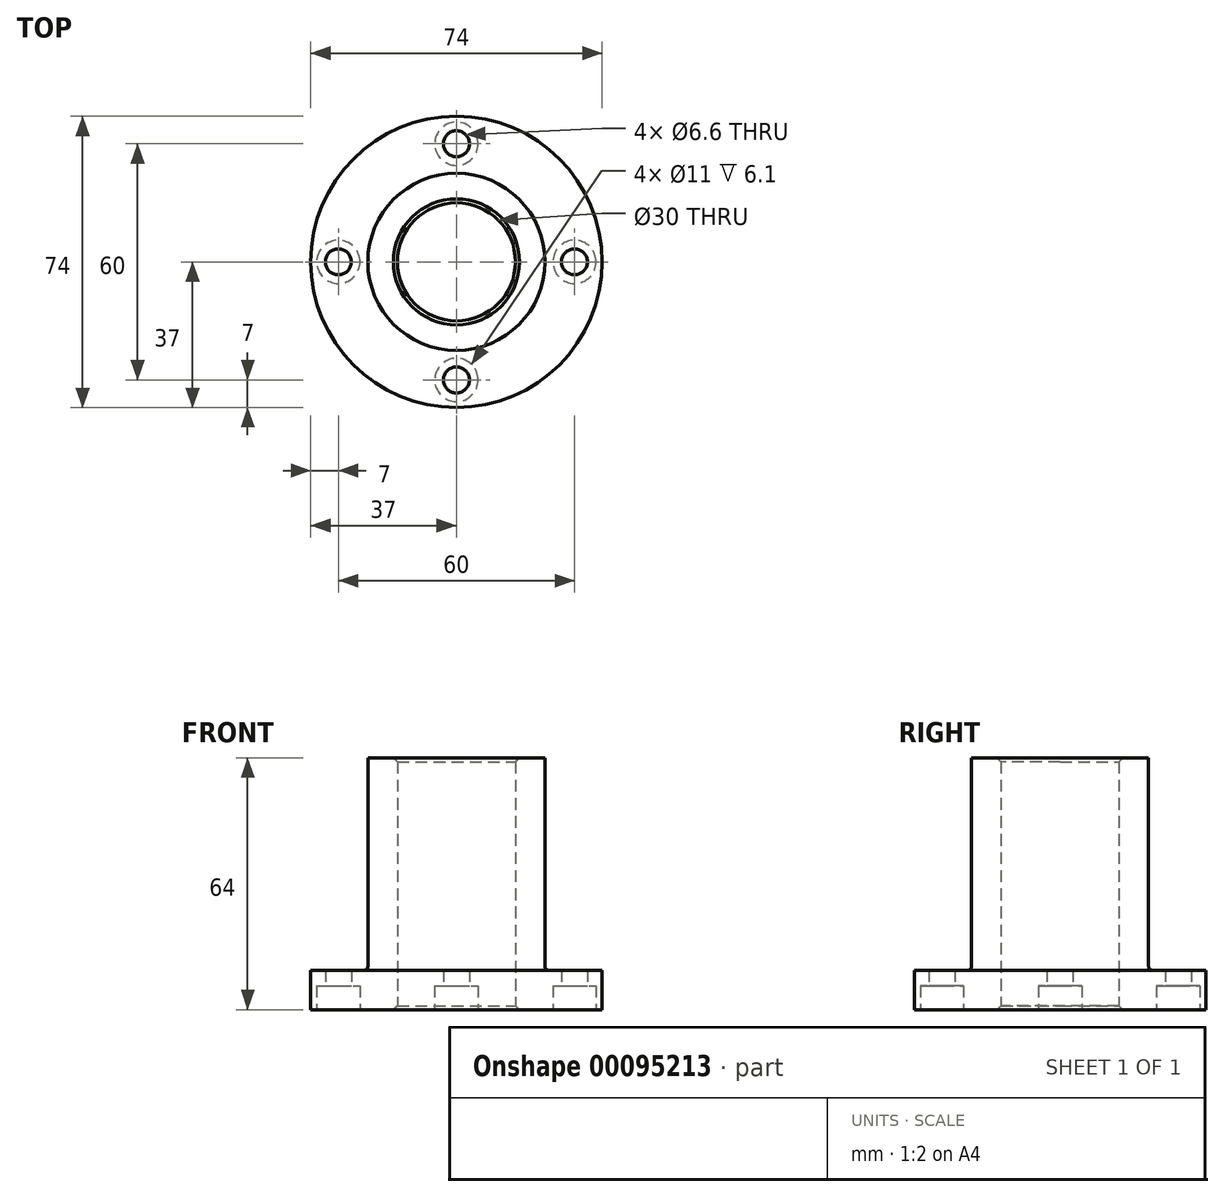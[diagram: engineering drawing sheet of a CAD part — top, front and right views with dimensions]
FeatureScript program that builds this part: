
annotation { "Feature Type Name" : "Feature", "Feature Type Description" : "" }
export const myFeature = defineFeature(function(context is Context, id is Id, definition is map)
    precondition{}
    {
        {
            var Q0;
            Q0=qCreatedBy(makeId("Front.planeOp"),FACE);
            var sketch = newSketch(context, id + "F0", { "sketchPlane" : qUnion([Q0])});
            skLineSegment(sketch, "E0", {"start": v(0, 0) * mm, "end": v(0, 87.58) * mm, "construction": true});
            skLineSegment(sketch, "E1", {"start": v(15, 0) * mm, "end": v(37, 0) * mm});
            skLineSegment(sketch, "E2", {"start": v(37, 0) * mm, "end": v(37, 10) * mm});
            skLineSegment(sketch, "E3", {"start": v(37, 10) * mm, "end": v(22.5, 10) * mm});
            skLineSegment(sketch, "E4", {"start": v(22.5, 10) * mm, "end": v(22.5, 64) * mm});
            skLineSegment(sketch, "E5", {"start": v(22.5, 64) * mm, "end": v(15, 64) * mm});
            skLineSegment(sketch, "E6", {"start": v(15, 0) * mm, "end": v(15, 64) * mm});
            skSolve(sketch);
        }
        {
            var Q0;
            Q0 = qSketchRegion(id + "F0", true);
            var Q1;
            Q1=sQuery(id+"F0.wireOp",EDGE,"E0");
            revolve(context, id + "F1", {"entities" : qUnion([Q0]), "axis" : qUnion([Q1]), "revolveType" : RevolveType.FULL});
        }
        {
            var Q0;
            Q0=makeQuery(id+"F1.opRevolve","SWEPT_FACE",FACE,{"disambiguationData":[OSD([sQuery(id+"F0.wireOp",EDGE,"E1")])]});
            var sketch = newSketch(context, id + "F2", { "sketchPlane" : qUnion([Q0])});
            skCircle(sketch, "E7", {"center": v(0, 0) * mm, "radius": 30 * mm, "construction": true});
            skLineSegment(sketch, "E8", {"start": v(0, 0) * mm, "end": v(0, 30) * mm, "construction": true});
            skLineSegment(sketch, "E9", {"start": v(0, 0) * mm, "end": v(30, 0) * mm, "construction": true});
            skLineSegment(sketch, "E10", {"start": v(0, 0) * mm, "end": v(0, -30) * mm, "construction": true});
            skLineSegment(sketch, "E11", {"start": v(0, 0) * mm, "end": v(-30, 0) * mm, "construction": true});
            skCircle(sketch, "E12", {"center": v(0, 30) * mm, "radius": 3.3 * mm});
            skCircle(sketch, "E13", {"center": v(-30, 0) * mm, "radius": 3.3 * mm});
            skCircle(sketch, "E14", {"center": v(0, -30) * mm, "radius": 3.3 * mm});
            skCircle(sketch, "E15", {"center": v(30, 0) * mm, "radius": 3.3 * mm});
            skSolve(sketch);
        }
        {
            var Q0;
            Q0 = qSketchRegion(id + "F2", true);
            extrude(context, id + "F3", {"entities" : qUnion([Q0]), "operationType" : NewBodyOperationType.REMOVE, "endBound" : BoundingType.THROUGH_ALL, "oppositeDirection" : true, "depth" : 25 * mm});
        }
        {
            var Q0;
            Q0=makeQuery(id+"F1.opRevolve","SWEPT_FACE",FACE,{"disambiguationData":[OSD([sQuery(id+"F0.wireOp",EDGE,"E1")])]});
            var sketch = newSketch(context, id + "F4", { "sketchPlane" : qUnion([Q0])});
            skCircle(sketch, "E16", {"center": v(0, 30) * mm, "radius": 5.5 * mm});
            skCircle(sketch, "E17", {"center": v(30, 0) * mm, "radius": 5.5 * mm});
            skCircle(sketch, "E18", {"center": v(-30, 0) * mm, "radius": 5.5 * mm});
            skCircle(sketch, "E19", {"center": v(0, -30) * mm, "radius": 5.5 * mm});
            skSolve(sketch);
        }
        {
            var Q0;
            Q0 = qSketchRegion(id + "F4", true);
            extrude(context, id + "F5", {"entities" : qUnion([Q0]), "operationType" : NewBodyOperationType.REMOVE, "oppositeDirection" : true, "depth" : 6.1 * mm});
        }
        {
            var Q0;
            Q0=makeQuery(id+"F1.opRevolve","SWEPT_EDGE",EDGE,{"disambiguationData":[OSD([sQuery(id+"F0.wireOp",EDGE,"E3"),sQuery(id+"F0.wireOp",EDGE,"E4")])]});
            fillet(context, id + "F6", {"entities" : qUnion([Q0]), "radius" : 1 * mm, "tangentPropagation" : true, "allowEdgeOverflow" : false});
        }
        {
            var Q0;
            Q0=makeQuery(id+"F1.opRevolve","SWEPT_EDGE",EDGE,{"disambiguationData":[OSD([sQuery(id+"F0.wireOp",EDGE,"E1"),sQuery(id+"F0.wireOp",EDGE,"E6")])]});
            chamfer(context, id + "F7", {"entities" : qUnion([Q0]), "chamferType" : ChamferType.TWO_OFFSETS, "width1" : 1 * mm, "oppositeDirection" : false, "width2" : 1 * mm, "tangentPropagation" : true});
        }
        {
            var Q0;
            Q0=makeQuery(id+"F1.opRevolve","SWEPT_EDGE",EDGE,{"disambiguationData":[OSD([sQuery(id+"F0.wireOp",EDGE,"E5"),sQuery(id+"F0.wireOp",EDGE,"E6")])]});
            chamfer(context, id + "F8", {"entities" : qUnion([Q0]), "width" : 1 * mm, "tangentPropagation" : true});
        }
    });
